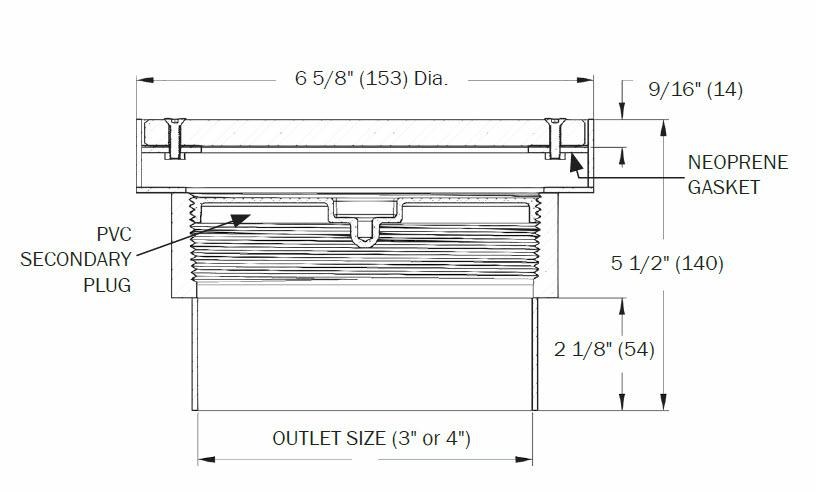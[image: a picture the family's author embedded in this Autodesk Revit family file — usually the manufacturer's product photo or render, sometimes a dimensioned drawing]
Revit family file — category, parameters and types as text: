
# Revit family: P7080-S
name_source: partatom
category: Plumbing Fixtures
revit_build: Autodesk Revit 2018 (Build: 20170223_1515(x64)
units: mm (PartAtom-declared; Revit-internal decimal feet)

## family parameters
Cut with Voids When Loaded = No
Host = Face
Part Type = Normal
Room Calculation Point = No
Round Connector Dimension = Use Radius
Shared = No

## types (3) — shared parameters
Default Elevation = 0' - 0"
Description = 8" SQUARE, TYPE 316 STAINLESS STEEL FABRICATED INDUSTRIAL FLOOR CLEANOUT
Floor Drain Material = Paint - Sherwin Williams Paint - #952C2A - Bellwood Red
MH-501 = No
MH-600 = No
Manufacturer = MIFAB
URL = WWW.MIFAB.COM
zero-valued in all types: CWFU, WFU

## per-type parameters (varying)
| type | MH-301 | MH-401 | Model | Pipe Diameter | Pipe Radius |
| P7083-S_Ø3" | Yes | No | P7083-S | 0' - 3" | 0' - 1 1/2" |
| P7084-S_Ø4" | No | Yes | P7084-S | 0' - 4" | 0' - 2" |
| P7086-S_Ø6" | No | Yes | P7086-S | 0' - 6" | 0' - 3" |

## geometry (parser evidence)
native form markers: Sweep x14
no freeform markers — native parametric forms only
